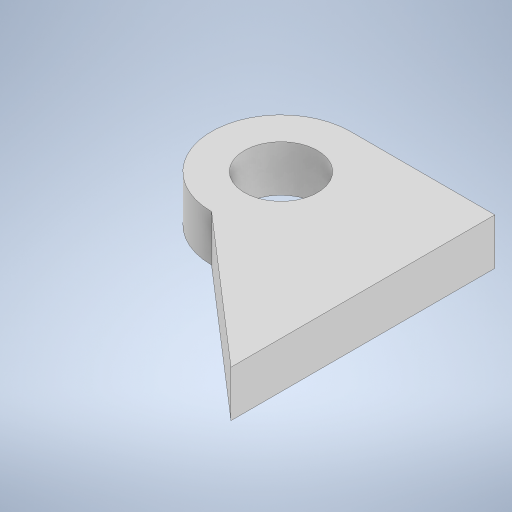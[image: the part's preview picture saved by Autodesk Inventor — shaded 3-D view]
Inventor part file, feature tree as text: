
AUTODESK INVENTOR PART (.ipt)
format: ipt  version: 2024 (Build 280153000, 153)  size: 225,792 bytes
history: native  units: mm
features: sketch x2, extrude x1
ambient origin geometry x8: Origin, YZ Plane, XZ Plane, XY Plane, X Axis, Y Axis, Z Axis, Center Point
bodies: Solid1 (feature_tree)
feature tree (3):
  extrude  "Extrusion1"  Depth=31.197mm
  sketch  "Sketch2"  dims[d2=42.0mm d4=10.0mm d5=0.0mm]
  sketch  "Sketch1"  dims[d0=15.8mm d1=31.197mm]
